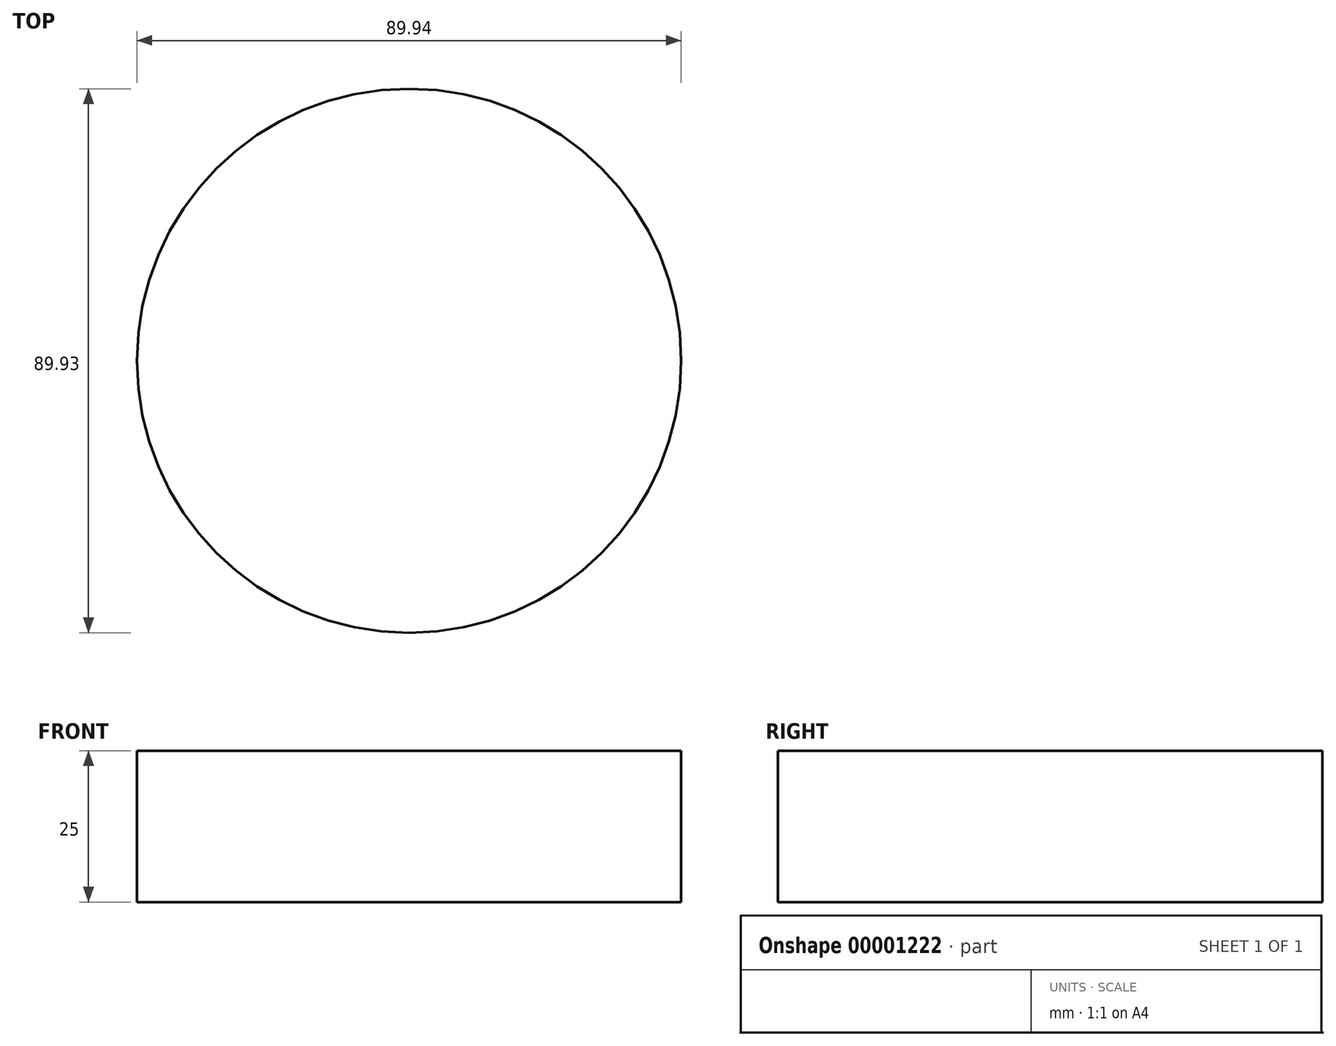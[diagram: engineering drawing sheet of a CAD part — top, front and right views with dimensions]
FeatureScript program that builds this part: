
annotation { "Feature Type Name" : "Feature", "Feature Type Description" : "" }
export const myFeature = defineFeature(function(context is Context, id is Id, definition is map)
    precondition{}
    {
        {
            var Q0;
            Q0=qCreatedBy(makeId("Top.planeOp"),FACE);
            var sketch = newSketch(context, id + "F0", { "sketchPlane" : qUnion([Q0])});
            skCircle(sketch, "E0", {"center": v(0, 17.83) * mm, "radius": 44.97 * mm});
            skSolve(sketch);
        }
        {
            var Q0;
            Q0=sQuery(id+"F0.wireOp",EDGE,"E0");
            extrude(context, id + "F1", {"bodyType" : ToolBodyType.SURFACE, "surfaceEntities" : qUnion([Q0]), "depth" : 25 * mm});
        }
    });
